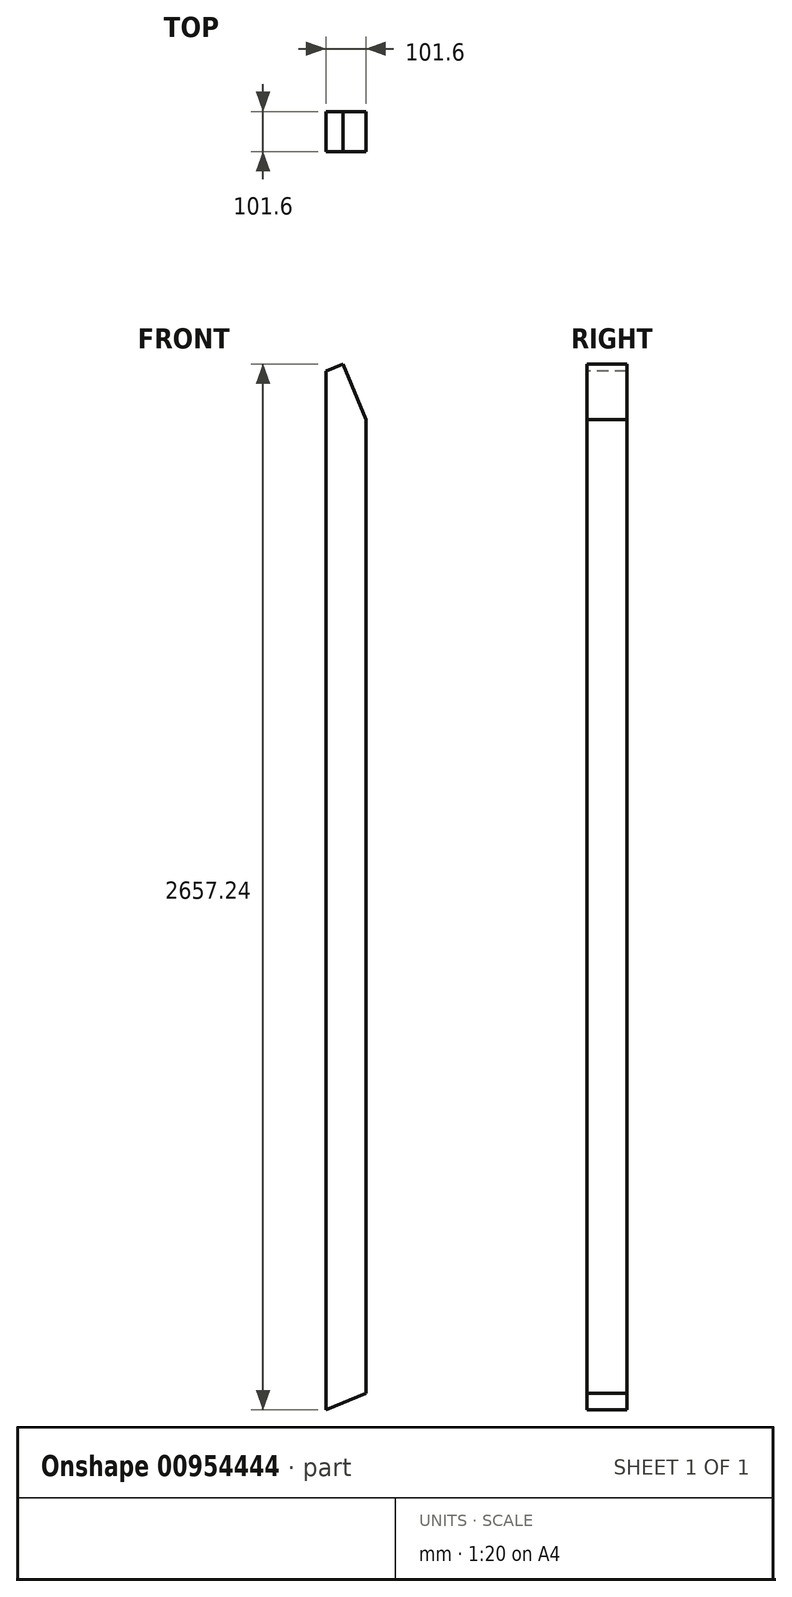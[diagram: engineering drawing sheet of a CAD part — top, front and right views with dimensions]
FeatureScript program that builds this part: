
annotation { "Feature Type Name" : "Feature", "Feature Type Description" : "" }
export const myFeature = defineFeature(function(context is Context, id is Id, definition is map)
    precondition{}
    {
        {
            var Q0;
            Q0=qCreatedBy(makeId("Top.planeOp"),FACE);
            var sketch = newSketch(context, id + "F0", { "sketchPlane" : qUnion([Q0])});
            skLineSegment(sketch, "E0.bottom", {"start": v(0, 0) * mm, "end": v(101.6, 0) * mm});
            skLineSegment(sketch, "E0.top", {"start": v(0, 101.6) * mm, "end": v(101.6, 101.6) * mm});
            skLineSegment(sketch, "E0.left", {"start": v(0, 0) * mm, "end": v(0, 101.6) * mm});
            skLineSegment(sketch, "E0.right", {"start": v(101.6, 0) * mm, "end": v(101.6, 101.6) * mm});
            skSolve(sketch);
        }
        {
            var Q0;
            Q0 = qSketchRegion(id + "F0", true);
            extrude(context, id + "F1", {"entities" : qUnion([Q0]), "depth" : 3048 * mm, "offsetDistance" : 25.4 * mm});
        }
        {
            var Q0;
            Q0=qCreatedBy(makeId("Front.planeOp"),FACE);
            var sketch = newSketch(context, id + "F2", { "sketchPlane" : qUnion([Q0])});
            skLineSegment(sketch, "E1", {"start": v(0, 0) * mm, "end": v(101.6, 42.08) * mm});
            skLineSegment(sketch, "E2", {"start": v(0, 0) * mm, "end": v(101.6, 0) * mm});
            skLineSegment(sketch, "E3", {"start": v(101.6, 0) * mm, "end": v(101.6, 42.08) * mm});
            skSolve(sketch);
        }
        {
            var Q0;
            Q0 = qSketchRegion(id + "F2", true);
            extrude(context, id + "F3", {"entities" : qUnion([Q0]), "operationType" : NewBodyOperationType.REMOVE, "endBound" : BoundingType.THROUGH_ALL, "oppositeDirection" : true, "depth" : 25.4 * mm, "offsetDistance" : 25.4 * mm});
        }
        {
            var Q0;
            Q0=makeQuery(id+"F1.opExtrude","SWEPT_FACE",FACE,{"disambiguationData":[OSD([sQuery(id+"F0.wireOp",EDGE,"E0.bottom")])]});
            var sketch = newSketch(context, id + "F4", { "sketchPlane" : qUnion([Q0])});
            skLineSegment(sketch, "E4", {"start": v(0, 2639.31) * mm, "end": v(101.6, 2681.4) * mm});
            skLineSegment(sketch, "E5", {"start": v(0, 2639.31) * mm, "end": v(0, 3048) * mm});
            skLineSegment(sketch, "E6", {"start": v(101.6, 3048) * mm, "end": v(101.6, 2681.4) * mm});
            skLineSegment(sketch, "E7", {"start": v(0, 3048) * mm, "end": v(101.6, 3048) * mm});
            skSolve(sketch);
        }
        {
            var Q0;
            Q0 = qSketchRegion(id + "F4", true);
            extrude(context, id + "F5", {"entities" : qUnion([Q0]), "operationType" : NewBodyOperationType.REMOVE, "endBound" : BoundingType.THROUGH_ALL, "oppositeDirection" : true, "depth" : 25.4 * mm, "offsetDistance" : 25.4 * mm});
        }
        {
            var Q0;
            Q0=makeQuery(id+"F1.opExtrude","SWEPT_FACE",FACE,{"disambiguationData":[OSD([sQuery(id+"F0.wireOp",EDGE,"E0.bottom")])]});
            var sketch = newSketch(context, id + "F6", { "sketchPlane" : qUnion([Q0])});
            skLineSegment(sketch, "E8", {"start": v(43.29, 2657.24) * mm, "end": v(101.6, 2516.46) * mm});
            skLineSegment(sketch, "E9", {"start": v(101.6, 2516.46) * mm, "end": v(101.6, 2681.4) * mm});
            skLineSegment(sketch, "E10", {"start": v(101.6, 2681.4) * mm, "end": v(43.29, 2657.24) * mm});
            skSolve(sketch);
        }
        {
            var Q0;
            Q0 = qSketchRegion(id + "F6", true);
            extrude(context, id + "F7", {"entities" : qUnion([Q0]), "operationType" : NewBodyOperationType.REMOVE, "endBound" : BoundingType.THROUGH_ALL, "oppositeDirection" : true, "depth" : 25.4 * mm, "offsetDistance" : 25.4 * mm});
        }
    });
